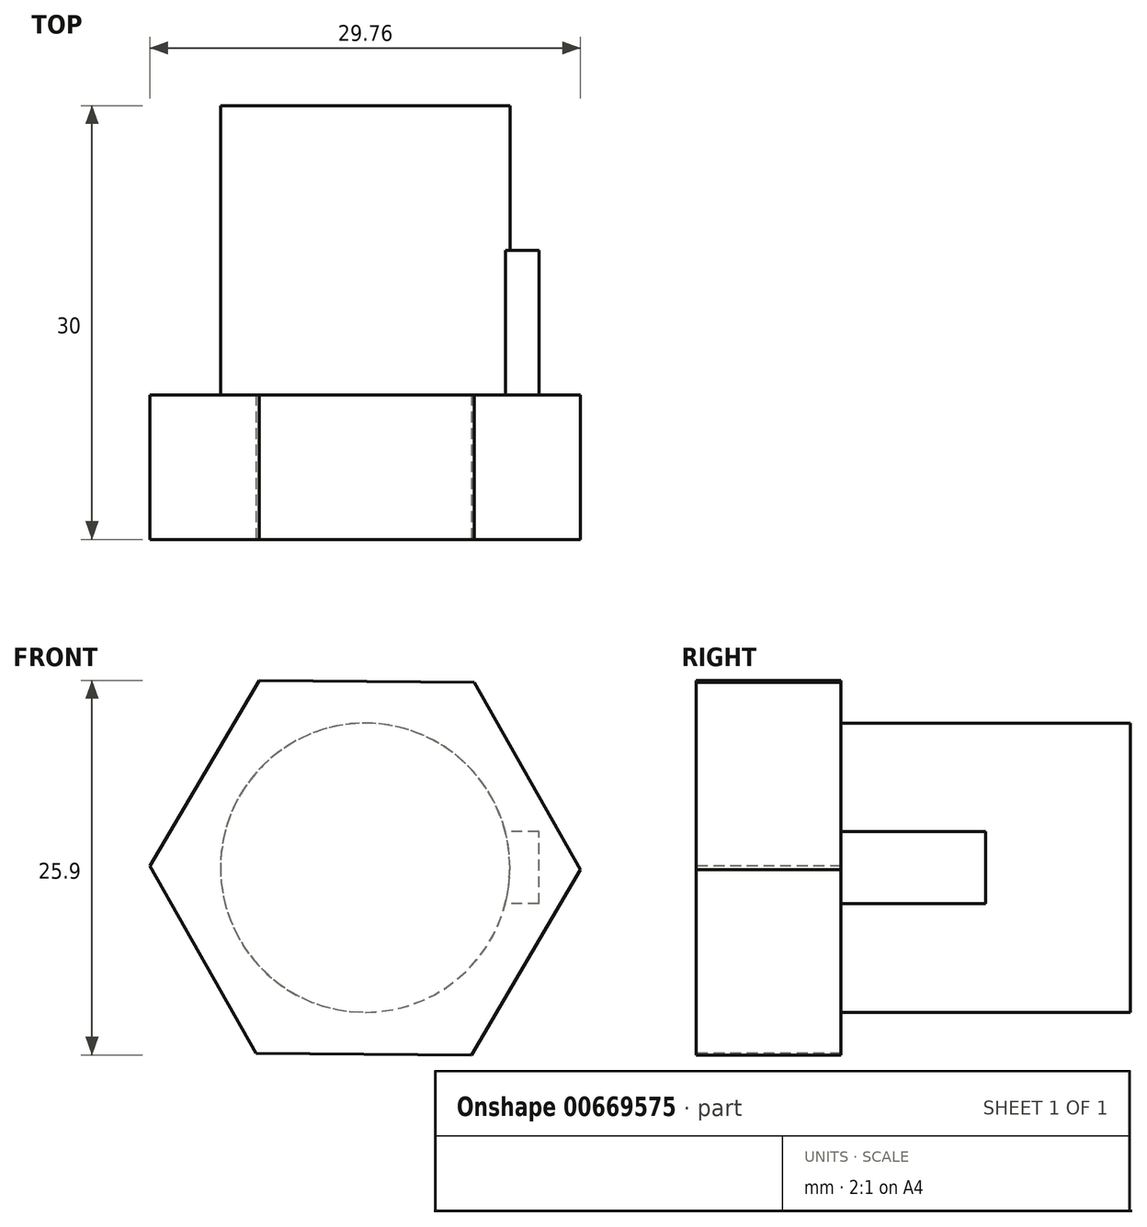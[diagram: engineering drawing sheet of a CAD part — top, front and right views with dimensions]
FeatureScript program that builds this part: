
annotation { "Feature Type Name" : "Feature", "Feature Type Description" : "" }
export const myFeature = defineFeature(function(context is Context, id is Id, definition is map)
    precondition{}
    {
        {
            var Q0;
            Q0=qCreatedBy(makeId("Front.planeOp"),FACE);
            var sketch = newSketch(context, id + "F0", { "sketchPlane" : qUnion([Q0])});
            skCircle(sketch, "E0", {"center": v(0, 0) * mm, "radius": 10 * mm});
            skLineSegment(sketch, "E1", {"start": v(12, -2.5) * mm, "end": v(9.68, -2.5) * mm});
            skLineSegment(sketch, "E2.0", {"start": v(7.33, -12.95) * mm, "end": v(-7.55, -12.82) * mm});
            skLineSegment(sketch, "E2.1", {"start": v(-7.55, -12.82) * mm, "end": v(-14.88, 0.12) * mm});
            skLineSegment(sketch, "E2.2", {"start": v(-14.88, 0.12) * mm, "end": v(-7.33, 12.95) * mm});
            skLineSegment(sketch, "E2.3", {"start": v(-7.33, 12.95) * mm, "end": v(7.55, 12.82) * mm});
            skLineSegment(sketch, "E2.4", {"start": v(7.55, 12.82) * mm, "end": v(14.88, -0.12) * mm});
            skLineSegment(sketch, "E2.5", {"start": v(14.88, -0.12) * mm, "end": v(7.33, -12.95) * mm});
            skLineSegment(sketch, "E3", {"start": v(12, -2.5) * mm, "end": v(12, 2.5) * mm});
            skLineSegment(sketch, "E4", {"start": v(12, 2.5) * mm, "end": v(9.68, 2.5) * mm});
            skSolve(sketch);
        }
        {
            var Q0;
            {var subQ0=sQuery(id+"F0.wireOp",EDGE,"E0");var subQ1=makeQuery(id+"F0.imprint","INTERSECT",VERTEX,{"derivedFrom":[subQ0,sQuery(id+"F0.wireOp",EDGE,"E1")]});Q0=makeQuery(id+"F0.imprint","IMPRINT",FACE,{"disambiguationData":[TD([[makeQuery(id+"F0.imprint","IMPRINT",EDGE,{"disambiguationData":[TD([[subQ1,1.0]])],"derivedFrom":subQ0}),1.0]])]});}
            var Q1;
            Q1=sQuery(id+"F0.wireOp",EDGE,"E0");
            extrude(context, id + "F1", {"entities" : qUnion([Q0]), "surfaceEntities" : qUnion([Q1]), "oppositeDirection" : true, "depth" : 30 * mm, "offsetDistance" : 25 * mm});
        }
        {
            var Q0;
            Q0=makeQuery(id+"F0.imprint","IMPRINT",FACE,{"disambiguationData":[TD([[makeQuery(id+"F0.imprint","IMPRINT",EDGE,{"derivedFrom":sQuery(id+"F0.wireOp",EDGE,"E0")}),-1.0]])]});
            var Q1;
            {var subQ0=sQuery(id+"F0.wireOp",EDGE,"E1");Q1=makeQuery(id+"F0.imprint","IMPRINT",FACE,{"disambiguationData":[TD([[makeQuery(id+"F0.imprint","IMPRINT",EDGE,{"derivedFrom":subQ0}),1.0]])]});}
            var Q2;
            Q2=sQuery(id+"F0.wireOp",EDGE,"E2.4");
            var Q3;
            Q3=sQuery(id+"F0.wireOp",EDGE,"E2.5");
            var Q4;
            Q4=sQuery(id+"F0.wireOp",EDGE,"E2.0");
            var Q5;
            Q5=sQuery(id+"F0.wireOp",EDGE,"E2.1");
            var Q6;
            Q6=sQuery(id+"F0.wireOp",EDGE,"E2.2");
            var Q7;
            Q7=sQuery(id+"F0.wireOp",EDGE,"E2.3");
            extrude(context, id + "F2", {"entities" : qUnion([Q0, Q1]), "operationType" : NewBodyOperationType.ADD, "surfaceEntities" : qUnion([Q2, Q3, Q4, Q5, Q6, Q7]), "oppositeDirection" : true, "depth" : 10 * mm, "offsetDistance" : 25 * mm});
        }
        {
            var Q0;
            {var subQ0=sQuery(id+"F0.wireOp",EDGE,"E1");Q0=makeQuery(id+"F0.imprint","IMPRINT",FACE,{"disambiguationData":[TD([[makeQuery(id+"F0.imprint","IMPRINT",EDGE,{"derivedFrom":subQ0}),-1.0]])]});}
            extrude(context, id + "F3", {"entities" : qUnion([Q0]), "operationType" : NewBodyOperationType.ADD, "oppositeDirection" : true, "depth" : 20 * mm, "offsetDistance" : 25 * mm});
        }
    });
